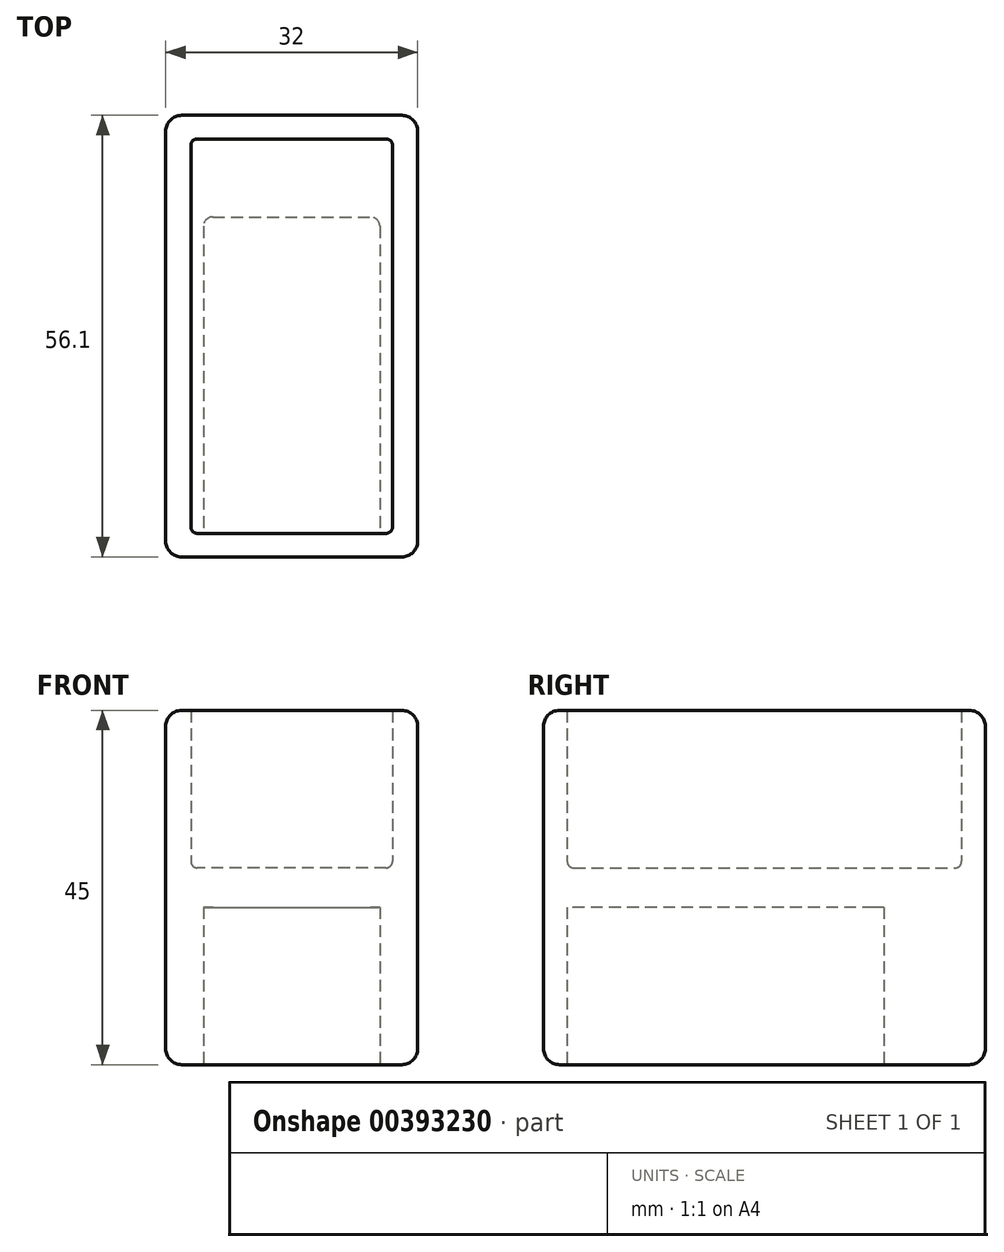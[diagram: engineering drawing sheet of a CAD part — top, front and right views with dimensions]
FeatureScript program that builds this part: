
annotation { "Feature Type Name" : "Feature", "Feature Type Description" : "" }
export const myFeature = defineFeature(function(context is Context, id is Id, definition is map)
    precondition{}
    {
        {
            var Q0;
            Q0=qCreatedBy(makeId("Top.planeOp"),FACE);
            var sketch = newSketch(context, id + "F0", { "sketchPlane" : qUnion([Q0])});
            skLineSegment(sketch, "E0.bottom", {"start": v(-16, 28.05) * mm, "end": v(16, 28.05) * mm});
            skLineSegment(sketch, "E0.top", {"start": v(-16, -28.05) * mm, "end": v(16, -28.05) * mm});
            skLineSegment(sketch, "E0.left", {"start": v(-16, 28.05) * mm, "end": v(-16, -28.05) * mm});
            skLineSegment(sketch, "E0.right", {"start": v(16, 28.05) * mm, "end": v(16, -28.05) * mm});
            skPoint(sketch, "E0.middle", {"position": v(0, 0) * mm});
            skLineSegment(sketch, "E1.bottom", {"start": v(-11.2, 15.15) * mm, "end": v(11.2, 15.15) * mm});
            skLineSegment(sketch, "E1.top", {"start": v(-11.2, -25.05) * mm, "end": v(11.2, -25.05) * mm});
            skLineSegment(sketch, "E1.left", {"start": v(-11.2, 15.15) * mm, "end": v(-11.2, -25.05) * mm});
            skLineSegment(sketch, "E1.right", {"start": v(11.2, 15.15) * mm, "end": v(11.2, -25.05) * mm});
            skLineSegment(sketch, "E2.bottom", {"start": v(12.8, -25.05) * mm, "end": v(-12.8, -25.05) * mm});
            skLineSegment(sketch, "E2.top", {"start": v(12.8, 25.05) * mm, "end": v(-12.8, 25.05) * mm});
            skLineSegment(sketch, "E2.left", {"start": v(12.8, -25.05) * mm, "end": v(12.8, 25.05) * mm});
            skLineSegment(sketch, "E2.right", {"start": v(-12.8, -25.05) * mm, "end": v(-12.8, 25.05) * mm});
            skSolve(sketch);
        }
        {
            var Q0;
            Q0=makeQuery(id+"F0.imprint","IMPRINT",FACE,{"disambiguationData":[TD([[makeQuery(id+"F0.imprint","IMPRINT",EDGE,{"derivedFrom":sQuery(id+"F0.wireOp",EDGE,"E1.bottom")}),1.0]])]});
            var Q1;
            Q1=makeQuery(id+"F0.imprint","IMPRINT",FACE,{"disambiguationData":[TD([[makeQuery(id+"F0.imprint","IMPRINT",EDGE,{"derivedFrom":sQuery(id+"F0.wireOp",EDGE,"E1.bottom")}),-1.0]])]});
            extrude(context, id + "F1", {"entities" : qUnion([Q0, Q1]), "depth" : 25 * mm});
        }
        {
            var Q0;
            Q0=makeQuery(id+"F0.imprint","IMPRINT",FACE,{"disambiguationData":[TD([[makeQuery(id+"F0.imprint","IMPRINT",EDGE,{"derivedFrom":sQuery(id+"F0.wireOp",EDGE,"E1.bottom")}),-1.0]])]});
            var Q1;
            Q1=makeQuery(id+"F0.imprint","IMPRINT",FACE,{"disambiguationData":[TD([[makeQuery(id+"F0.imprint","IMPRINT",EDGE,{"derivedFrom":sQuery(id+"F0.wireOp",EDGE,"E1.bottom")}),1.0]])]});
            extrude(context, id + "F2", {"entities" : qUnion([Q0, Q1]), "operationType" : NewBodyOperationType.REMOVE, "depth" : 20 * mm});
        }
        {
            var Q0;
            Q0=qSketchRegion(id+"F0",true);
            extrude(context, id + "F3", {"entities" : qUnion([Q0]), "operationType" : NewBodyOperationType.ADD, "depth" : 45 * mm});
        }
        {
            var Q0;
            Q0=makeQuery(id+"F0.imprint","IMPRINT",FACE,{"disambiguationData":[TD([[makeQuery(id+"F0.imprint","IMPRINT",EDGE,{"derivedFrom":sQuery(id+"F0.wireOp",EDGE,"E1.bottom")}),1.0]])]});
            extrude(context, id + "F4", {"entities" : qUnion([Q0]), "operationType" : NewBodyOperationType.ADD, "depth" : 20 * mm});
        }
        {
            var Q0;
            Q0=makeQuery(id+"F3.opExtrude","SWEPT_FACE",FACE,{"disambiguationData":[OSD([sQuery(id+"F0.wireOp",EDGE,"E0.right")])]});
            var Q1;
            Q1=makeQuery(id+"F3.opExtrude","SWEPT_FACE",FACE,{"disambiguationData":[OSD([sQuery(id+"F0.wireOp",EDGE,"E0.left")])]});
            var Q2;
            Q2=makeQuery(id+"F3.opExtrude","SWEPT_FACE",FACE,{"disambiguationData":[OSD([sQuery(id+"F0.wireOp",EDGE,"E0.bottom")])]});
            var Q3;
            Q3=makeQuery(id+"F3.opExtrude","SWEPT_FACE",FACE,{"disambiguationData":[OSD([sQuery(id+"F0.wireOp",EDGE,"E0.top")])]});
            var Q4;
            Q4=makeQuery(id+"F1.opExtrude","SWEPT_EDGE",EDGE,{"disambiguationData":[OSD([sQuery(id+"F0.wireOp",EDGE,"E0.top"),sQuery(id+"F0.wireOp",EDGE,"E0.right")])]});
            var Q5;
            Q5=makeQuery(id+"F1.opExtrude","SWEPT_EDGE",EDGE,{"disambiguationData":[OSD([sQuery(id+"F0.wireOp",EDGE,"E0.bottom"),sQuery(id+"F0.wireOp",EDGE,"E0.right")])]});
            var Q6;
            Q6=makeQuery(id+"F1.opExtrude","SWEPT_EDGE",EDGE,{"disambiguationData":[OSD([sQuery(id+"F0.wireOp",EDGE,"E0.bottom"),sQuery(id+"F0.wireOp",EDGE,"E0.left")])]});
            var Q7;
            Q7=makeQuery(id+"F1.opExtrude","SWEPT_EDGE",EDGE,{"disambiguationData":[OSD([sQuery(id+"F0.wireOp",EDGE,"E0.top"),sQuery(id+"F0.wireOp",EDGE,"E0.left")])]});
            fillet(context, id + "F5", {"entities" : qUnion([Q0, Q1, Q2, Q3, Q4, Q5, Q6, Q7]), "radius" : 2 * mm, "tangentPropagation" : true, "allowEdgeOverflow" : false});
        }
        {
            var Q0;
            Q0=makeQuery(id+"F3.opExtrude","SWEPT_EDGE",EDGE,{"disambiguationData":[OSD([sQuery(id+"F0.wireOp",EDGE,"E2.top"),sQuery(id+"F0.wireOp",EDGE,"E2.left")])]});
            var Q1;
            Q1=makeQuery(id+"F3.opExtrude","SWEPT_EDGE",EDGE,{"disambiguationData":[OSD([sQuery(id+"F0.wireOp",EDGE,"E2.bottom"),sQuery(id+"F0.wireOp",EDGE,"E2.left")])]});
            var Q2;
            Q2=makeQuery(id+"F3.opExtrude","SWEPT_EDGE",EDGE,{"disambiguationData":[OSD([sQuery(id+"F0.wireOp",EDGE,"E2.bottom"),sQuery(id+"F0.wireOp",EDGE,"E2.right")])]});
            var Q3;
            Q3=makeQuery(id+"F3.opExtrude","SWEPT_EDGE",EDGE,{"disambiguationData":[OSD([sQuery(id+"F0.wireOp",EDGE,"E2.top"),sQuery(id+"F0.wireOp",EDGE,"E2.right")])]});
            var Q4;
            Q4=makeQuery(id+"F1.opExtrude","CAP_FACE",FACE,{"disambiguationData":[OSD([sQuery(id+"F0.wireOp",EDGE,"E2.bottom"),sQuery(id+"F0.wireOp",EDGE,"E2.top"),sQuery(id+"F0.wireOp",EDGE,"E2.left"),sQuery(id+"F0.wireOp",EDGE,"E2.right")])],"isStart":false});
            fillet(context, id + "F6", {"entities" : qUnion([Q0, Q1, Q2, Q3, Q4]), "radius" : 0.8 * mm, "tangentPropagation" : true, "allowEdgeOverflow" : false});
        }
        {
            var Q0;
            Q0=makeQuery(id+"F4.opExtrude","SWEPT_EDGE",EDGE,{"disambiguationData":[OSD([sQuery(id+"F0.wireOp",EDGE,"E1.left"),sQuery(id+"F0.wireOp",EDGE,"E2.bottom")])]});
            var Q1;
            Q1=makeQuery(id+"F4.opExtrude","SWEPT_EDGE",EDGE,{"disambiguationData":[OSD([sQuery(id+"F0.wireOp",EDGE,"E1.right"),sQuery(id+"F0.wireOp",EDGE,"E2.bottom")])]});
            var Q2;
            Q2=makeQuery(id+"F4.opExtrude","SWEPT_EDGE",EDGE,{"disambiguationData":[OSD([sQuery(id+"F0.wireOp",EDGE,"E1.bottom"),sQuery(id+"F0.wireOp",EDGE,"E1.right")])]});
            var Q3;
            Q3=makeQuery(id+"F4.opExtrude","SWEPT_EDGE",EDGE,{"disambiguationData":[OSD([sQuery(id+"F0.wireOp",EDGE,"E1.bottom"),sQuery(id+"F0.wireOp",EDGE,"E1.left")])]});
            fillet(context, id + "F7", {"entities" : qUnion([Q0, Q1, Q2, Q3]), "radius" : 1.2 * mm, "tangentPropagation" : true, "allowEdgeOverflow" : false});
        }
    });
